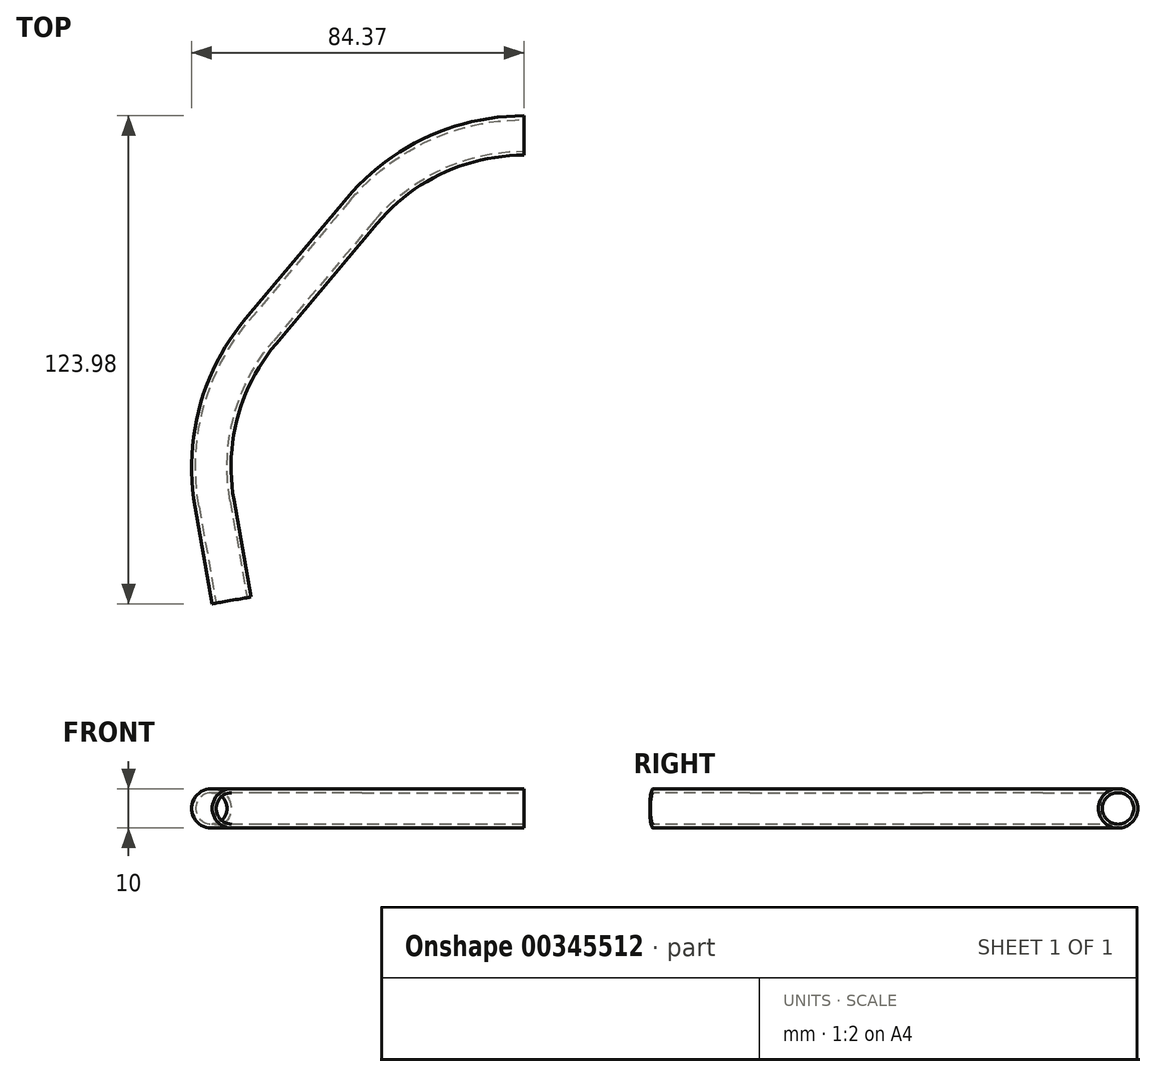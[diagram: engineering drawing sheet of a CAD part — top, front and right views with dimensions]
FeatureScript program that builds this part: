
annotation { "Feature Type Name" : "Feature", "Feature Type Description" : "" }
export const myFeature = defineFeature(function(context is Context, id is Id, definition is map)
    precondition{}
    {
        {
            var Q0;
            Q0=qCreatedBy(makeId("Top.planeOp"),FACE);
            var sketch = newSketch(context, id + "F0", { "sketchPlane" : qUnion([Q0])});
            skArc(sketch, "E0", {"start": v(0, 0) * mm, "mid": v(-22.66, -5.02) * mm, "end": v(-41.08, -19.14) * mm});
            skArc(sketch, "E1", {"start": v(-78.56, -93.52) * mm, "mid": v(-77.54, -70.34) * mm, "end": v(-66.82, -49.76) * mm});
            skLineSegment(sketch, "E2", {"start": v(-66.82, -49.76) * mm, "end": v(-41.08, -19.14) * mm});
            skLineSegment(sketch, "E3", {"start": v(-78.56, -93.52) * mm, "end": v(-74.23, -118.12) * mm});
            skSolve(sketch);
        }
        {
            var Q0;
            Q0=qCreatedBy(makeId("Right.planeOp"),FACE);
            var sketch = newSketch(context, id + "F1", { "sketchPlane" : qUnion([Q0])});
            skCircle(sketch, "E4", {"center": v(0, 0) * mm, "radius": 4 * mm});
            skCircle(sketch, "E5", {"center": v(0, 0) * mm, "radius": 5 * mm});
            skSolve(sketch);
        }
        {
            var Q0;
            Q0=makeQuery(id+"F1.imprint","IMPRINT",FACE,{"disambiguationData":[TD([[makeQuery(id+"F1.imprint","IMPRINT",EDGE,{"derivedFrom":sQuery(id+"F1.wireOp",EDGE,"E4")}),-1.0]])]});
            var Q1;
            Q1=sQuery(id+"F0.wireOp",EDGE,"E0");
            var Q2;
            Q2=sQuery(id+"F0.wireOp",EDGE,"E2");
            var Q3;
            Q3=sQuery(id+"F0.wireOp",EDGE,"E1");
            var Q4;
            Q4=sQuery(id+"F0.wireOp",EDGE,"E3");
            sweep(context, id + "F2", {"profiles" : qUnion([Q0]), "path" : qUnion([Q1, Q2, Q3, Q4])});
        }
    });
